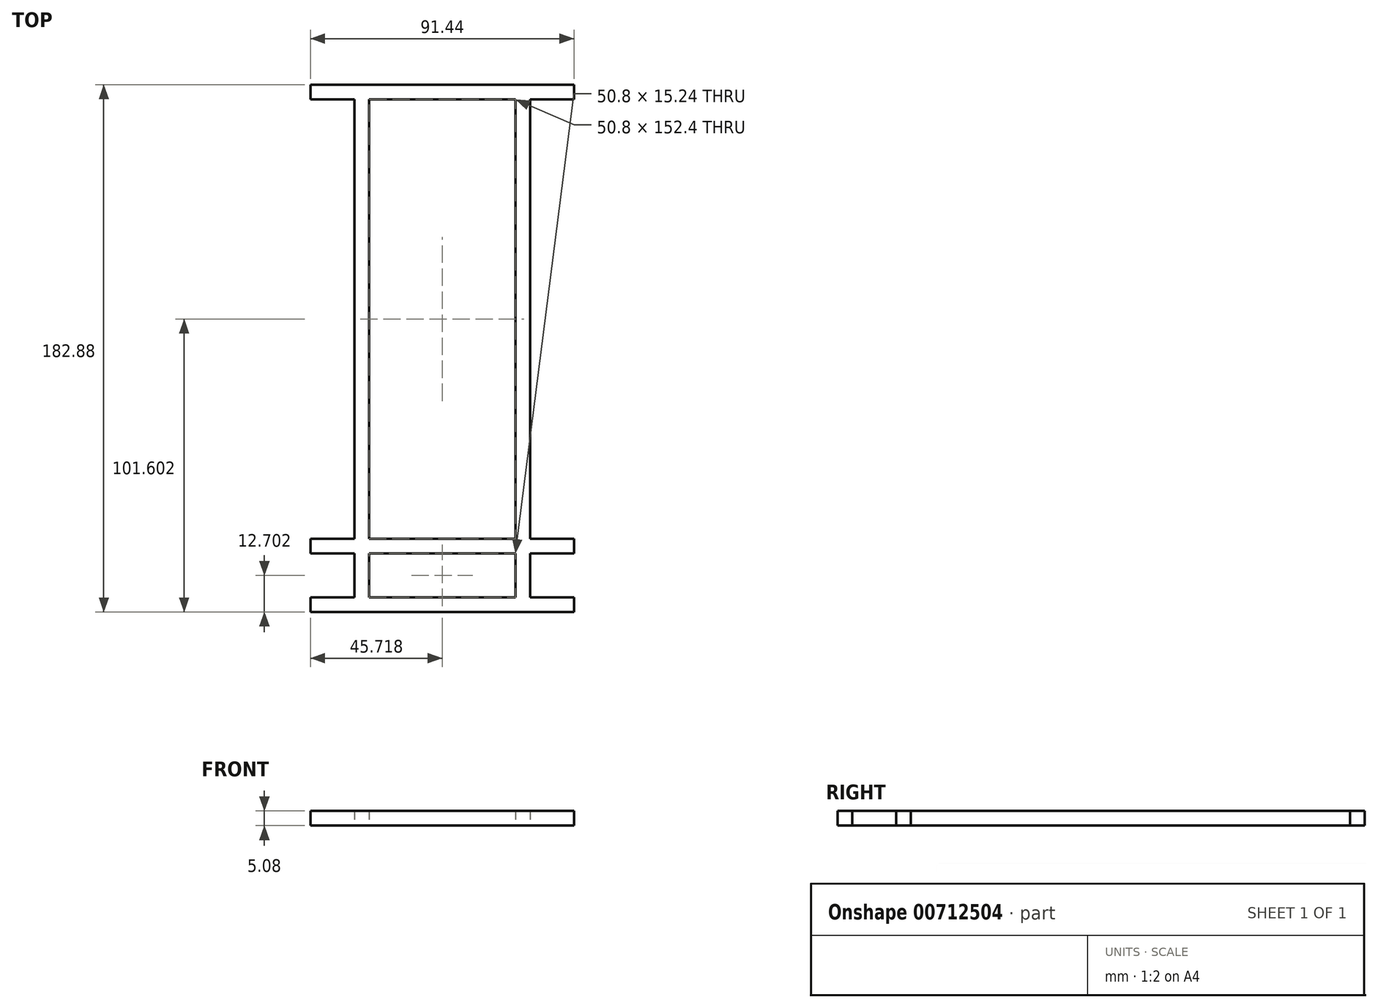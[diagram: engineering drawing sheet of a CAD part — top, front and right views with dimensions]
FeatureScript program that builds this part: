
annotation { "Feature Type Name" : "Feature", "Feature Type Description" : "" }
export const myFeature = defineFeature(function(context is Context, id is Id, definition is map)
    precondition{}
    {
        {
            var Q0;
            Q0=qCreatedBy(makeId("Top.planeOp"),FACE);
            var sketch = newSketch(context, id + "F0", { "sketchPlane" : qUnion([Q0])});
            skLineSegment(sketch, "E0.bottom", {"start": v(-76.82, 94.14) * mm, "end": v(-71.74, 94.14) * mm});
            skLineSegment(sketch, "E0.top", {"start": v(-76.82, -88.74) * mm, "end": v(-71.74, -88.74) * mm});
            skLineSegment(sketch, "E0.left", {"start": v(-76.82, 94.14) * mm, "end": v(-76.82, -88.74) * mm});
            skLineSegment(sketch, "E0.right", {"start": v(-71.74, 94.14) * mm, "end": v(-71.74, -88.74) * mm});
            skLineSegment(sketch, "E1.bottom", {"start": v(-92.06, 94.14) * mm, "end": v(-0.62, 94.14) * mm});
            skLineSegment(sketch, "E1.top", {"start": v(-92.06, 89.06) * mm, "end": v(-0.62, 89.06) * mm});
            skLineSegment(sketch, "E1.left", {"start": v(-92.06, 94.14) * mm, "end": v(-92.06, 89.06) * mm});
            skLineSegment(sketch, "E1.right", {"start": v(-0.62, 94.14) * mm, "end": v(-0.62, 89.06) * mm});
            skLineSegment(sketch, "E2.bottom", {"start": v(-20.94, 94.14) * mm, "end": v(-15.86, 94.14) * mm});
            skLineSegment(sketch, "E2.top", {"start": v(-20.94, -88.74) * mm, "end": v(-15.86, -88.74) * mm});
            skLineSegment(sketch, "E2.left", {"start": v(-20.94, 94.14) * mm, "end": v(-20.94, -88.74) * mm});
            skLineSegment(sketch, "E2.right", {"start": v(-15.86, 94.14) * mm, "end": v(-15.86, -88.74) * mm});
            skLineSegment(sketch, "E3.bottom", {"start": v(-92.06, -83.66) * mm, "end": v(-0.62, -83.66) * mm});
            skLineSegment(sketch, "E3.top", {"start": v(-92.06, -88.74) * mm, "end": v(-0.62, -88.74) * mm});
            skLineSegment(sketch, "E3.left", {"start": v(-92.06, -83.66) * mm, "end": v(-92.06, -88.74) * mm});
            skLineSegment(sketch, "E3.right", {"start": v(-0.62, -83.66) * mm, "end": v(-0.62, -88.74) * mm});
            skSolve(sketch);
        }
        {
            var Q0;
            Q0 = qSketchRegion(id + "F0", true);
            extrude(context, id + "F1", {"entities" : qUnion([Q0]), "depth" : 5.08 * mm, "offsetDistance" : 25.4 * mm});
        }
        {
            var Q0;
            Q0=makeQuery(id+"F1.opExtrude","SWEPT_FACE",FACE,{"disambiguationData":[OSD([sQuery(id+"F0.wireOp",EDGE,"E0.right")])]});
            var sketch = newSketch(context, id + "F2", { "sketchPlane" : qUnion([Q0])});
            skLineSegment(sketch, "E4.bottom", {"start": v(-68.42, 5.08) * mm, "end": v(-63.34, 5.08) * mm});
            skLineSegment(sketch, "E4.top", {"start": v(-68.42, 0) * mm, "end": v(-63.34, 0) * mm});
            skLineSegment(sketch, "E4.left", {"start": v(-68.42, 5.08) * mm, "end": v(-68.42, 0) * mm});
            skLineSegment(sketch, "E4.right", {"start": v(-63.34, 5.08) * mm, "end": v(-63.34, 0) * mm});
            skSolve(sketch);
        }
        {
            var Q0;
            Q0 = qSketchRegion(id + "F2", true);
            extrude(context, id + "F3", {"entities" : qUnion([Q0]), "operationType" : NewBodyOperationType.ADD, "depth" : 50.8 * mm, "offsetDistance" : 25.4 * mm});
        }
        {
            var Q0;
            Q0=makeQuery(id+"F1.opExtrude","SWEPT_FACE",FACE,{"disambiguationData":[OSD([sQuery(id+"F0.wireOp",EDGE,"E2.right")])]});
            var sketch = newSketch(context, id + "F4", { "sketchPlane" : qUnion([Q0])});
            skLineSegment(sketch, "E5.bottom", {"start": v(-68.42, 5.08) * mm, "end": v(-63.34, 5.08) * mm});
            skLineSegment(sketch, "E5.top", {"start": v(-68.42, 0) * mm, "end": v(-63.34, 0) * mm});
            skLineSegment(sketch, "E5.left", {"start": v(-68.42, 5.08) * mm, "end": v(-68.42, 0) * mm});
            skLineSegment(sketch, "E5.right", {"start": v(-63.34, 5.08) * mm, "end": v(-63.34, 0) * mm});
            skSolve(sketch);
        }
        {
            var Q0;
            Q0 = qSketchRegion(id + "F4", true);
            extrude(context, id + "F5", {"entities" : qUnion([Q0]), "operationType" : NewBodyOperationType.ADD, "depth" : 15.24 * mm, "offsetDistance" : 25.4 * mm});
        }
        {
            var Q0;
            Q0=makeQuery(id+"F1.opExtrude","SWEPT_FACE",FACE,{"disambiguationData":[OSD([sQuery(id+"F0.wireOp",EDGE,"E0.left")])]});
            var sketch = newSketch(context, id + "F6", { "sketchPlane" : qUnion([Q0])});
            skLineSegment(sketch, "E6.bottom", {"start": v(68.42, 5.08) * mm, "end": v(63.34, 5.08) * mm});
            skLineSegment(sketch, "E6.top", {"start": v(68.42, 0) * mm, "end": v(63.34, 0) * mm});
            skLineSegment(sketch, "E6.left", {"start": v(68.42, 5.08) * mm, "end": v(68.42, 0) * mm});
            skLineSegment(sketch, "E6.right", {"start": v(63.34, 5.08) * mm, "end": v(63.34, 0) * mm});
            skSolve(sketch);
        }
        {
            var Q0;
            Q0 = qSketchRegion(id + "F6", true);
            extrude(context, id + "F7", {"entities" : qUnion([Q0]), "operationType" : NewBodyOperationType.ADD, "depth" : 15.24 * mm, "offsetDistance" : 25.4 * mm});
        }
    });
